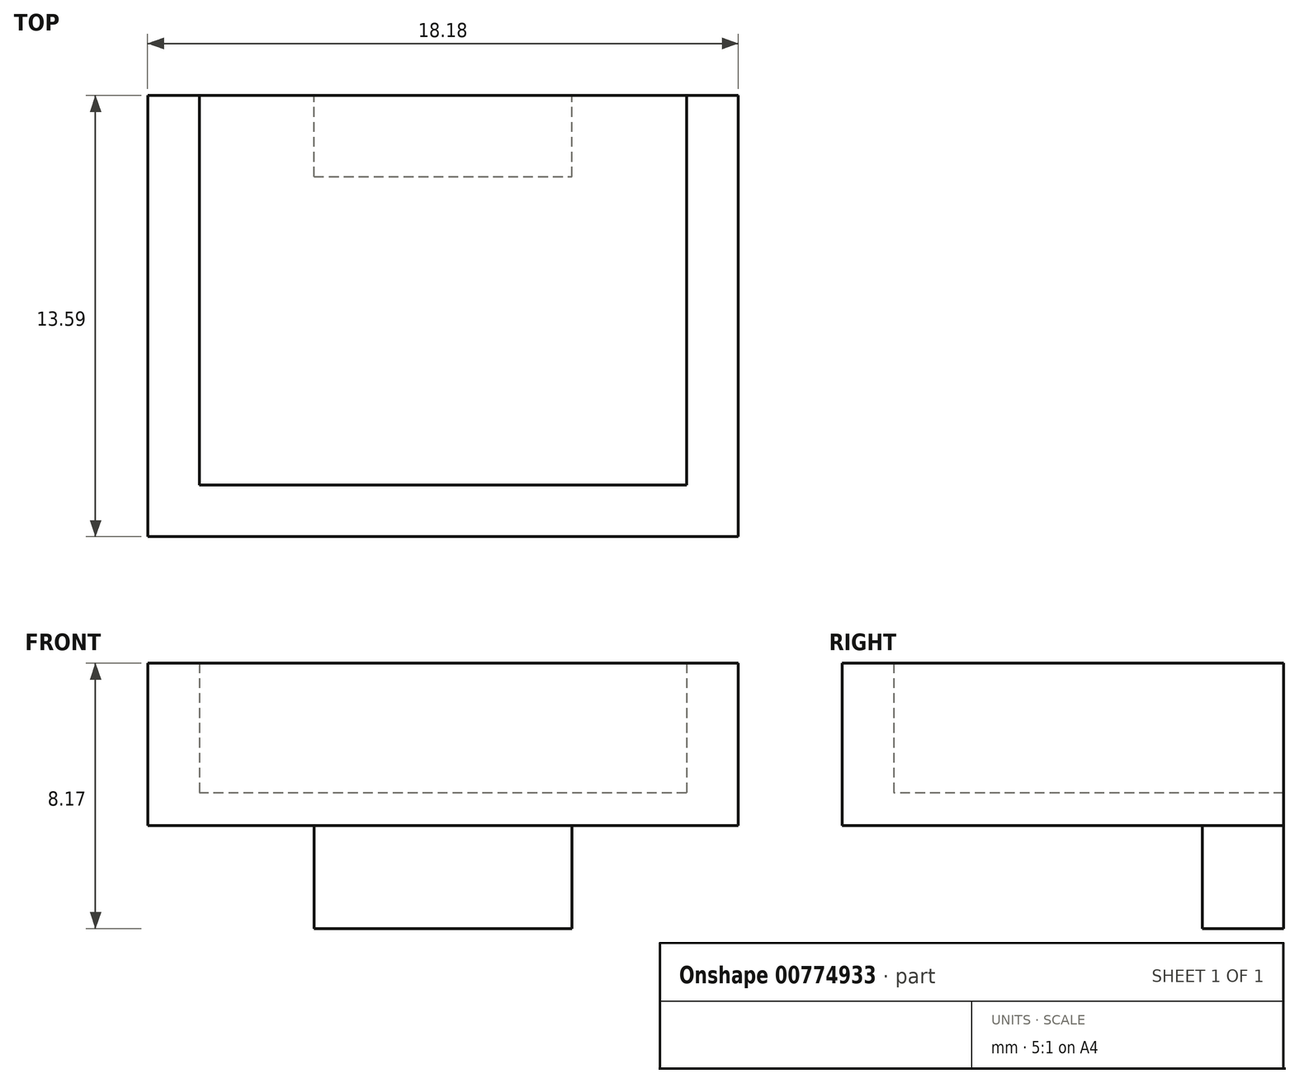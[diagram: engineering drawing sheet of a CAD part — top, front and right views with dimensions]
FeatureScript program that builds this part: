
annotation { "Feature Type Name" : "Feature", "Feature Type Description" : "" }
export const myFeature = defineFeature(function(context is Context, id is Id, definition is map)
    precondition{}
    {
        {
            var Q0;
            Q0=qCreatedBy(makeId("Top.planeOp"),FACE);
            var sketch = newSketch(context, id + "F0", { "sketchPlane" : qUnion([Q0])});
            skLineSegment(sketch, "E0.top", {"start": v(7.5, -6) * mm, "end": v(-7.5, -6) * mm});
            skLineSegment(sketch, "E0.left", {"start": v(7.5, 6) * mm, "end": v(7.5, -6) * mm});
            skLineSegment(sketch, "E0.right", {"start": v(-7.5, 6) * mm, "end": v(-7.5, -6) * mm});
            skPoint(sketch, "E0.middle", {"position": v(0, 0) * mm});
            skLineSegment(sketch, "E1", {"start": v(-7.5, 6) * mm, "end": v(7.5, 6) * mm});
            skLineSegment(sketch, "E2.bottom", {"start": v(7.5, 6) * mm, "end": v(9.09, 6) * mm});
            skLineSegment(sketch, "E2.top", {"start": v(7.5, -7.59) * mm, "end": v(9.09, -7.59) * mm});
            skLineSegment(sketch, "E2.left", {"start": v(7.5, 6) * mm, "end": v(7.5, -7.59) * mm});
            skLineSegment(sketch, "E2.right", {"start": v(9.09, 6) * mm, "end": v(9.09, -7.59) * mm});
            skLineSegment(sketch, "E3.MirrorCS", {"start": v(-6, 6) * mm, "end": v(-7.59, 6) * mm});
            skLineSegment(sketch, "E4.MirrorCS", {"start": v(-7.5, -6) * mm, "end": v(4.5, -6) * mm});
            skLineSegment(sketch, "E5.MirrorCS", {"start": v(-7.5, 6) * mm, "end": v(-9.09, 6) * mm});
            skLineSegment(sketch, "E6.MirrorCS", {"start": v(-9.09, 6) * mm, "end": v(-9.09, -7.59) * mm});
            skLineSegment(sketch, "E7.MirrorCS", {"start": v(-7.5, -7.59) * mm, "end": v(-9.09, -7.59) * mm});
            skLineSegment(sketch, "E8.MirrorCS", {"start": v(-7.5, 6) * mm, "end": v(-7.5, -7.59) * mm});
            skLineSegment(sketch, "E9.bottom", {"start": v(-7.5, -7.59) * mm, "end": v(7.5, -7.59) * mm});
            skLineSegment(sketch, "E9.top", {"start": v(-7.5, -6) * mm, "end": v(7.5, -6) * mm});
            skLineSegment(sketch, "E9.left", {"start": v(-7.5, -7.59) * mm, "end": v(-7.5, -6) * mm});
            skLineSegment(sketch, "E9.right", {"start": v(7.5, -7.59) * mm, "end": v(7.5, -6) * mm});
            skLineSegment(sketch, "E10.bottom", {"start": v(-7.5, 6) * mm, "end": v(-5.47, 6) * mm});
            skLineSegment(sketch, "E10.left", {"start": v(-7.5, 6) * mm, "end": v(-7.5, 4.41) * mm});
            skLineSegment(sketch, "E11.bottom", {"start": v(-3.97, 3.5) * mm, "end": v(3.97, 3.5) * mm});
            skLineSegment(sketch, "E11.top", {"start": v(-3.97, 6) * mm, "end": v(3.97, 6) * mm});
            skLineSegment(sketch, "E11.left", {"start": v(-3.97, 3.5) * mm, "end": v(-3.97, 6) * mm});
            skLineSegment(sketch, "E12", {"start": v(3.97, 3.5) * mm, "end": v(3.97, 6) * mm});
            skSolve(sketch);
        }
        {
            var Q0;
            Q0=makeQuery(id+"F0.imprint","IMPRINT",FACE,{"disambiguationData":[TD([[makeQuery(id+"F0.imprint","IMPRINT",EDGE,{"derivedFrom":sQuery(id+"F0.wireOp",EDGE,"E2.bottom")}),-1.0]])]});
            var Q1;
            Q1=makeQuery(id+"F0.imprint","IMPRINT",FACE,{"disambiguationData":[TD([[makeQuery(id+"F0.imprint","IMPRINT",EDGE,{"derivedFrom":sQuery(id+"F0.wireOp",EDGE,"E9.bottom")}),1.0]])]});
            var Q2;
            Q2=makeQuery(id+"F0.imprint","IMPRINT",FACE,{"disambiguationData":[TD([[makeQuery(id+"F0.imprint","IMPRINT",EDGE,{"derivedFrom":sQuery(id+"F0.wireOp",EDGE,"E5.MirrorCS")}),1.0]])]});
            extrude(context, id + "F1", {"entities" : qUnion([Q0, Q1, Q2]), "depth" : 5 * mm, "offsetDistance" : 25.4 * mm});
        }
        {
            var Q0;
            Q0 = qSketchRegion(id + "F0", true);
            extrude(context, id + "F2", {"entities" : qUnion([Q0]), "operationType" : NewBodyOperationType.ADD, "depth" : 1 * mm, "offsetDistance" : 25.4 * mm});
        }
        {
            var Q0;
            Q0=makeQuery(id+"F0.imprint","IMPRINT",FACE,{"disambiguationData":[TD([[makeQuery(id+"F0.imprint","IMPRINT",EDGE,{"derivedFrom":sQuery(id+"F0.wireOp",EDGE,"E11.bottom")}),1.0]])]});
            extrude(context, id + "F3", {"entities" : qUnion([Q0]), "operationType" : NewBodyOperationType.ADD, "oppositeDirection" : true, "depth" : 3.17 * mm, "offsetDistance" : 25.4 * mm});
        }
    });
